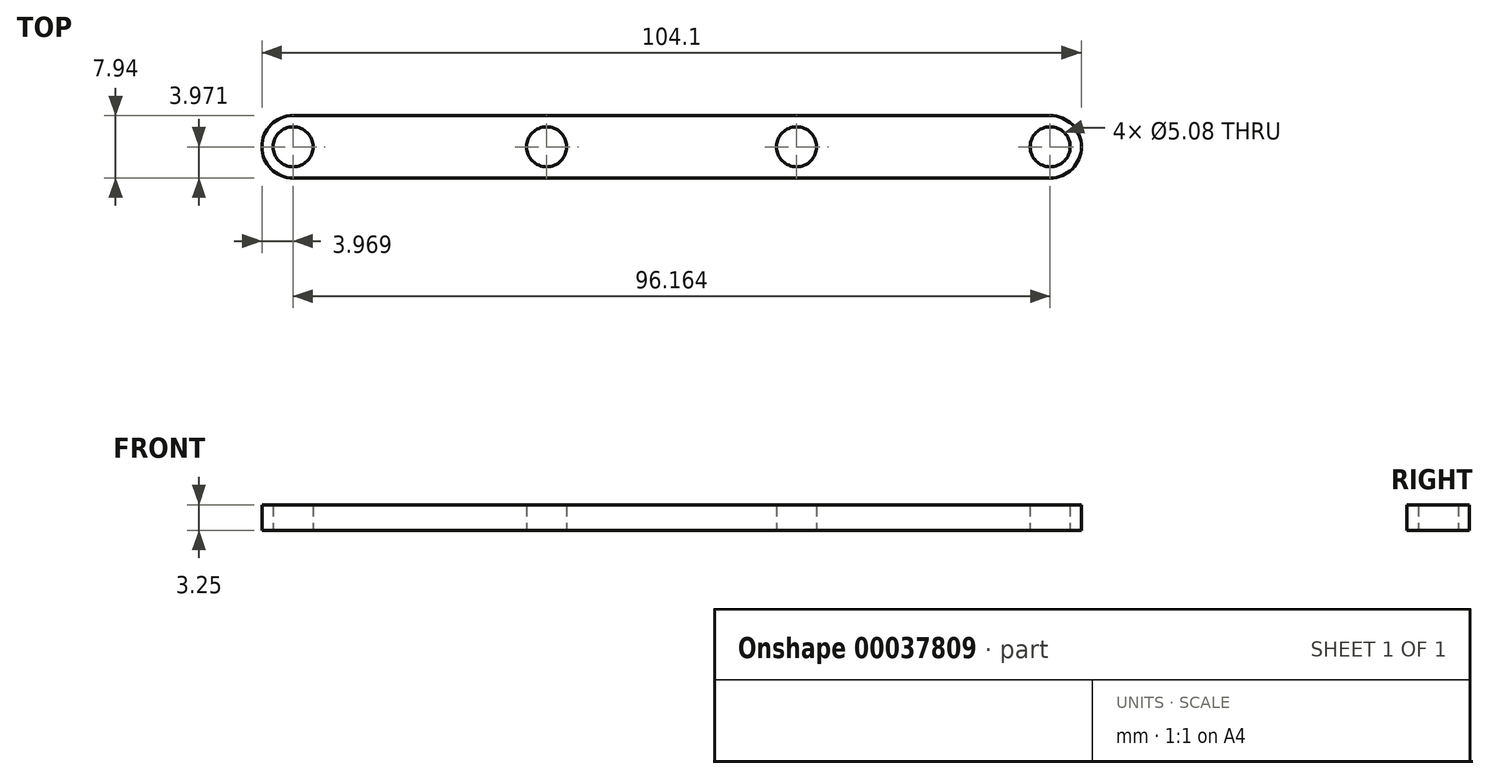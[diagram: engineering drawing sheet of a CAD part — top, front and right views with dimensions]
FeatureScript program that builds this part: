
annotation { "Feature Type Name" : "Feature", "Feature Type Description" : "" }
export const myFeature = defineFeature(function(context is Context, id is Id, definition is map)
    precondition{}
    {
        {
            var Q0;
            Q0=qCreatedBy(makeId("Top.planeOp"),FACE);
            var sketch = newSketch(context, id + "F0", { "sketchPlane" : qUnion([Q0])});
            skLineSegment(sketch, "E0.bottom", {"start": v(0, 0) * mm, "end": v(104.1, 0) * mm});
            skLineSegment(sketch, "E0.top", {"start": v(0, -7.94) * mm, "end": v(104.1, -7.94) * mm});
            skLineSegment(sketch, "E0.left", {"start": v(0, 0) * mm, "end": v(0, -7.94) * mm});
            skLineSegment(sketch, "E0.right", {"start": v(104.1, 0) * mm, "end": v(104.1, -7.94) * mm});
            skLineSegment(sketch, "E1", {"start": v(0, -3.97) * mm, "end": v(3.97, -3.97) * mm, "construction": true});
            skLineSegment(sketch, "E2", {"start": v(3.97, -3.97) * mm, "end": v(36.18, -3.97) * mm, "construction": true});
            skLineSegment(sketch, "E3", {"start": v(36.18, -3.97) * mm, "end": v(67.93, -3.97) * mm, "construction": true});
            skLineSegment(sketch, "E4", {"start": v(67.93, -3.97) * mm, "end": v(100.13, -3.97) * mm, "construction": true});
            skLineSegment(sketch, "E5", {"start": v(100.13, -3.97) * mm, "end": v(104.1, -3.97) * mm, "construction": true});
            skCircle(sketch, "E6", {"center": v(3.97, -3.97) * mm, "radius": 2.54 * mm});
            skCircle(sketch, "E7", {"center": v(36.18, -3.97) * mm, "radius": 2.54 * mm});
            skCircle(sketch, "E8", {"center": v(67.93, -3.97) * mm, "radius": 2.54 * mm});
            skCircle(sketch, "E9", {"center": v(100.13, -3.97) * mm, "radius": 2.54 * mm});
            skSolve(sketch);
        }
        {
            var Q0;
            Q0=qSketchRegion(id+"F0",true);
            extrude(context, id + "F1", {"entities" : qUnion([Q0]), "depth" : 3.25 * mm});
        }
        {
            var Q0;
            Q0=makeQuery(id+"F1.opExtrude","SWEPT_EDGE",EDGE,{"disambiguationData":[OSD([sQuery(id+"F0.wireOp",EDGE,"E0.bottom"),sQuery(id+"F0.wireOp",EDGE,"E0.left")])]});
            var Q1;
            Q1=makeQuery(id+"F1.opExtrude","SWEPT_EDGE",EDGE,{"disambiguationData":[OSD([sQuery(id+"F0.wireOp",EDGE,"E0.top"),sQuery(id+"F0.wireOp",EDGE,"E0.left")])]});
            var Q2;
            Q2=makeQuery(id+"F1.opExtrude","SWEPT_EDGE",EDGE,{"disambiguationData":[OSD([sQuery(id+"F0.wireOp",EDGE,"E0.top"),sQuery(id+"F0.wireOp",EDGE,"E0.right")])]});
            var Q3;
            Q3=makeQuery(id+"F1.opExtrude","SWEPT_EDGE",EDGE,{"disambiguationData":[OSD([sQuery(id+"F0.wireOp",EDGE,"E0.bottom"),sQuery(id+"F0.wireOp",EDGE,"E0.right")])]});
            fillet(context, id + "F2", {"entities" : qUnion([Q0, Q1, Q2, Q3]), "radius" : 3.97 * mm, "tangentPropagation" : true, "allowEdgeOverflow" : false});
        }
    });
